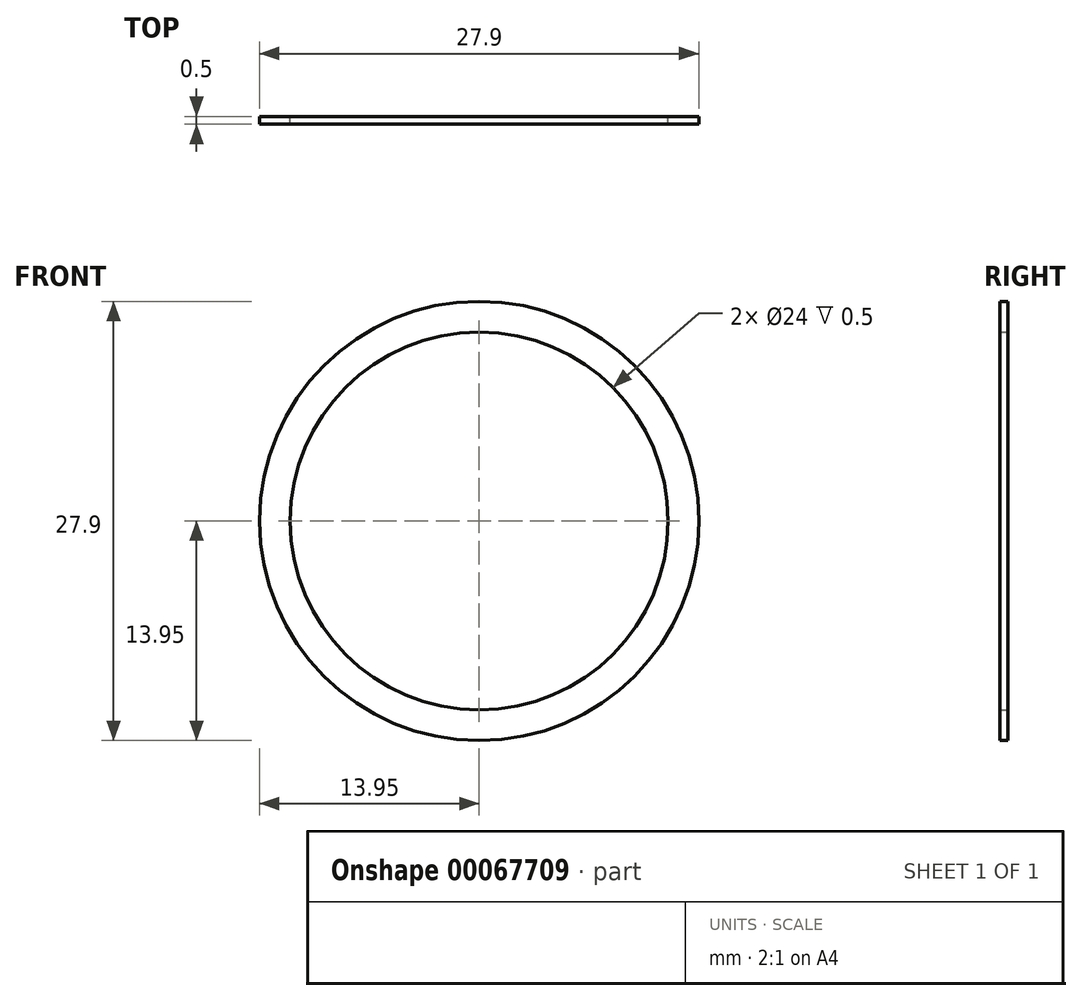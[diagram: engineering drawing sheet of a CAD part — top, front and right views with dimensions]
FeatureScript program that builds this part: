
annotation { "Feature Type Name" : "Feature", "Feature Type Description" : "" }
export const myFeature = defineFeature(function(context is Context, id is Id, definition is map)
    precondition{}
    {
        {
            var Q0;
            Q0=qCreatedBy(makeId("Front.planeOp"),FACE);
            var sketch = newSketch(context, id + "F0", { "sketchPlane" : qUnion([Q0])});
            skCircle(sketch, "E0", {"center": v(0, 0) * mm, "radius": 13.95 * mm});
            skCircle(sketch, "E1", {"center": v(0, 0) * mm, "radius": 12 * mm});
            skSolve(sketch);
        }
        {
            var Q0;
            Q0=makeQuery(id+"F0.imprint","IMPRINT",FACE,{"disambiguationData":[TD([[makeQuery(id+"F0.imprint","IMPRINT",EDGE,{"derivedFrom":sQuery(id+"F0.wireOp",EDGE,"E0")}),1.0]])]});
            extrude(context, id + "F1", {"entities" : qUnion([Q0]), "depth" : 0.5 * mm});
        }
    });
